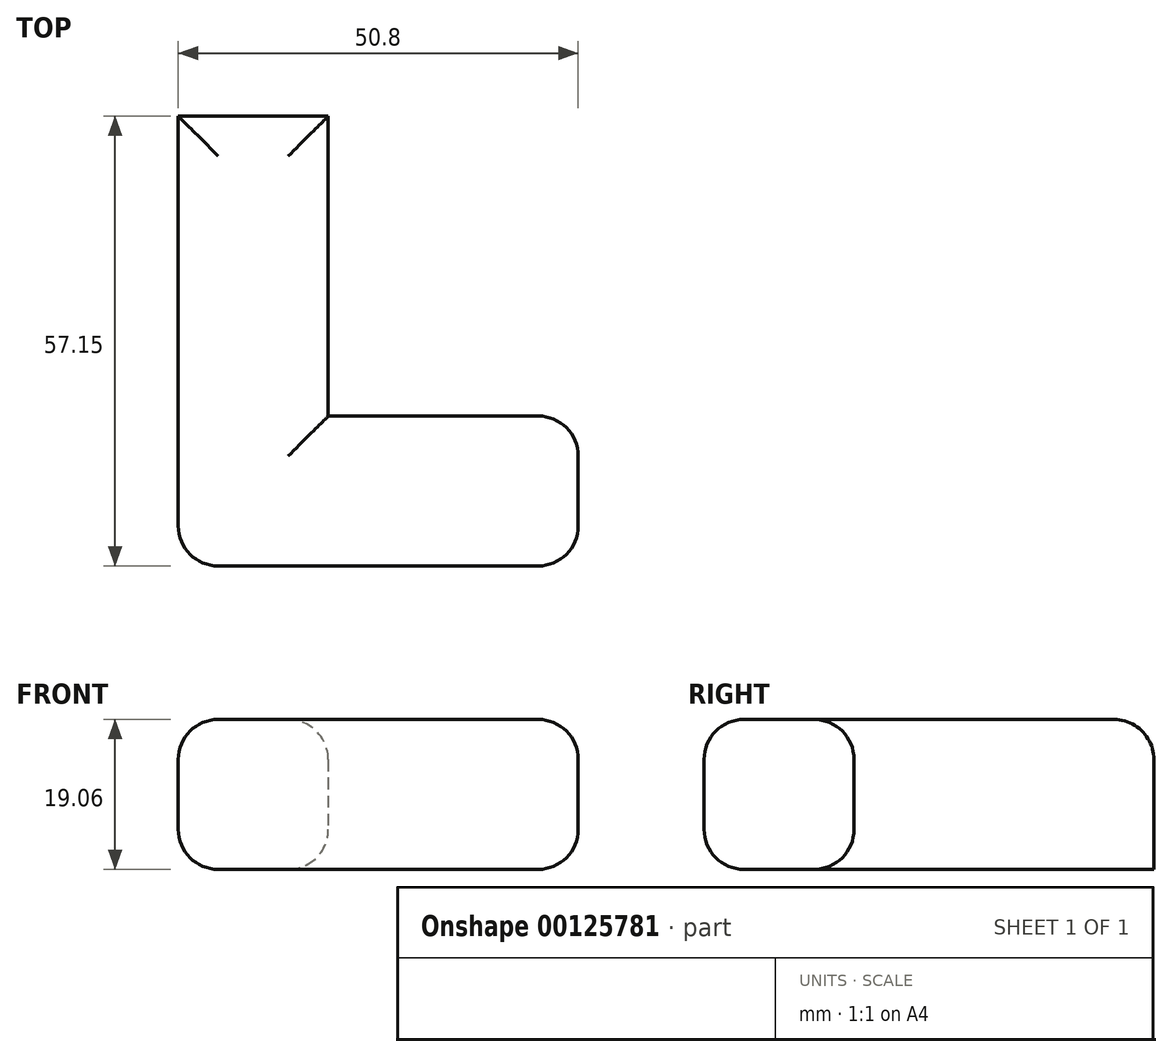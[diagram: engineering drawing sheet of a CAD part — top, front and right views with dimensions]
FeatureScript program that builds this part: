
annotation { "Feature Type Name" : "Feature", "Feature Type Description" : "" }
export const myFeature = defineFeature(function(context is Context, id is Id, definition is map)
    precondition{}
    {
        {
            var Q0;
            Q0=qCreatedBy(makeId("Top.planeOp"),FACE);
            var sketch = newSketch(context, id + "F0", { "sketchPlane" : qUnion([Q0])});
            skLineSegment(sketch, "E0.bottom", {"start": v(9.53, -28.58) * mm, "end": v(-9.52, -28.58) * mm});
            skLineSegment(sketch, "E0.top", {"start": v(9.52, 28.58) * mm, "end": v(-9.53, 28.58) * mm});
            skLineSegment(sketch, "E0.left", {"start": v(9.53, -28.57) * mm, "end": v(9.52, 28.58) * mm});
            skLineSegment(sketch, "E0.right", {"start": v(-9.52, -28.58) * mm, "end": v(-9.53, 28.58) * mm});
            skPoint(sketch, "E0.middle", {"position": v(0, 0) * mm});
            skSolve(sketch);
        }
        {
            var Q0;
            Q0 = qSketchRegion(id + "F0", true);
            extrude(context, id + "F1", {"entities" : qUnion([Q0]), "endBound" : BoundingType.SYMMETRIC, "depth" : 19.05 * mm});
        }
        {
            var Q0;
            Q0=makeQuery(id+"F1.opExtrude","SWEPT_FACE",FACE,{"disambiguationData":[OSD([sQuery(id+"F0.wireOp",EDGE,"E0.left")])]});
            var sketch = newSketch(context, id + "F2", { "sketchPlane" : qUnion([Q0])});
            skLineSegment(sketch, "E1.bottom", {"start": v(-28.58, 9.53) * mm, "end": v(-9.53, 9.53) * mm});
            skLineSegment(sketch, "E1.top", {"start": v(-28.58, -9.53) * mm, "end": v(-9.53, -9.53) * mm});
            skLineSegment(sketch, "E1.left", {"start": v(-28.58, 9.53) * mm, "end": v(-28.58, -9.53) * mm});
            skLineSegment(sketch, "E1.right", {"start": v(-9.53, 9.53) * mm, "end": v(-9.53, -9.53) * mm});
            skSolve(sketch);
        }
        {
            var Q0;
            Q0 = qSketchRegion(id + "F2", true);
            extrude(context, id + "F3", {"entities" : qUnion([Q0]), "operationType" : NewBodyOperationType.ADD, "depth" : 31.75 * mm});
        }
        {
            var Q0;
            Q0=makeQuery(id+"F1.opExtrude","CAP_EDGE",EDGE,{"disambiguationData":[OSD([sQuery(id+"F0.wireOp",EDGE,"E0.left")])],"isStart":false});
            var Q1;
            Q1=makeQuery(id+"F3.boolean.opBoolean","MERGE",FACE,{"derivedFrom":[makeQuery(id+"F1.opExtrude","CAP_FACE",FACE,{"disambiguationData":[OSD([sQuery(id+"F0.wireOp",EDGE,"E0.bottom"),sQuery(id+"F0.wireOp",EDGE,"E0.top"),sQuery(id+"F0.wireOp",EDGE,"E0.left"),sQuery(id+"F0.wireOp",EDGE,"E0.right")])],"isStart":false}),makeQuery(id+"F3.opExtrude","SWEPT_FACE",FACE,{"disambiguationData":[OSD([sQuery(id+"F2.wireOp",EDGE,"E1.bottom")])]})]});
            var Q2;
            Q2=makeQuery(id+"F3.boolean.opBoolean","MERGE",EDGE,{"derivedFrom":[makeQuery(id+"F1.opExtrude","CAP_EDGE",EDGE,{"disambiguationData":[OSD([sQuery(id+"F0.wireOp",EDGE,"E0.bottom")])],"isStart":true}),makeQuery(id+"F3.opExtrude","SWEPT_EDGE",EDGE,{"disambiguationData":[OSD([sQuery(id+"F2.wireOp",EDGE,"E1.top"),sQuery(id+"F2.wireOp",EDGE,"E1.left")])]})]});
            var Q3;
            Q3=makeQuery(id+"F3.opExtrude","CAP_EDGE",EDGE,{"disambiguationData":[OSD([sQuery(id+"F2.wireOp",EDGE,"E1.left")])],"isStart":false});
            var Q4;
            Q4=makeQuery(id+"F3.opExtrude","CAP_EDGE",EDGE,{"disambiguationData":[OSD([sQuery(id+"F2.wireOp",EDGE,"E1.right")])],"isStart":false});
            var Q5;
            Q5=makeQuery(id+"F3.opExtrude","CAP_EDGE",EDGE,{"disambiguationData":[OSD([sQuery(id+"F2.wireOp",EDGE,"E1.top")])],"isStart":false});
            var Q6;
            Q6=makeQuery(id+"F1.opExtrude","CAP_EDGE",EDGE,{"disambiguationData":[OSD([sQuery(id+"F0.wireOp",EDGE,"E0.right")])],"isStart":true});
            var Q7;
            Q7=makeQuery(id+"F1.opExtrude","SWEPT_EDGE",EDGE,{"disambiguationData":[OSD([sQuery(id+"F0.wireOp",EDGE,"E0.bottom"),sQuery(id+"F0.wireOp",EDGE,"E0.right")])]});
            var Q8;
            Q8=makeQuery(id+"F1.opExtrude","CAP_EDGE",EDGE,{"disambiguationData":[OSD([sQuery(id+"F0.wireOp",EDGE,"E0.left")])],"isStart":true});
            var Q9;
            Q9=makeQuery(id+"F3.opExtrude","SWEPT_EDGE",EDGE,{"disambiguationData":[OSD([sQuery(id+"F0.wireOp",EDGE,"E0.left"),sQuery(id+"F2.wireOp",EDGE,"E1.top"),sQuery(id+"F2.wireOp",EDGE,"E1.right")])]});
            fillet(context, id + "F4", {"entities" : qUnion([Q0, Q1, Q2, Q3, Q4, Q5, Q6, Q7, Q8, Q9]), "radius" : 5.08 * mm, "tangentPropagation" : true, "allowEdgeOverflow" : false});
        }
    });
